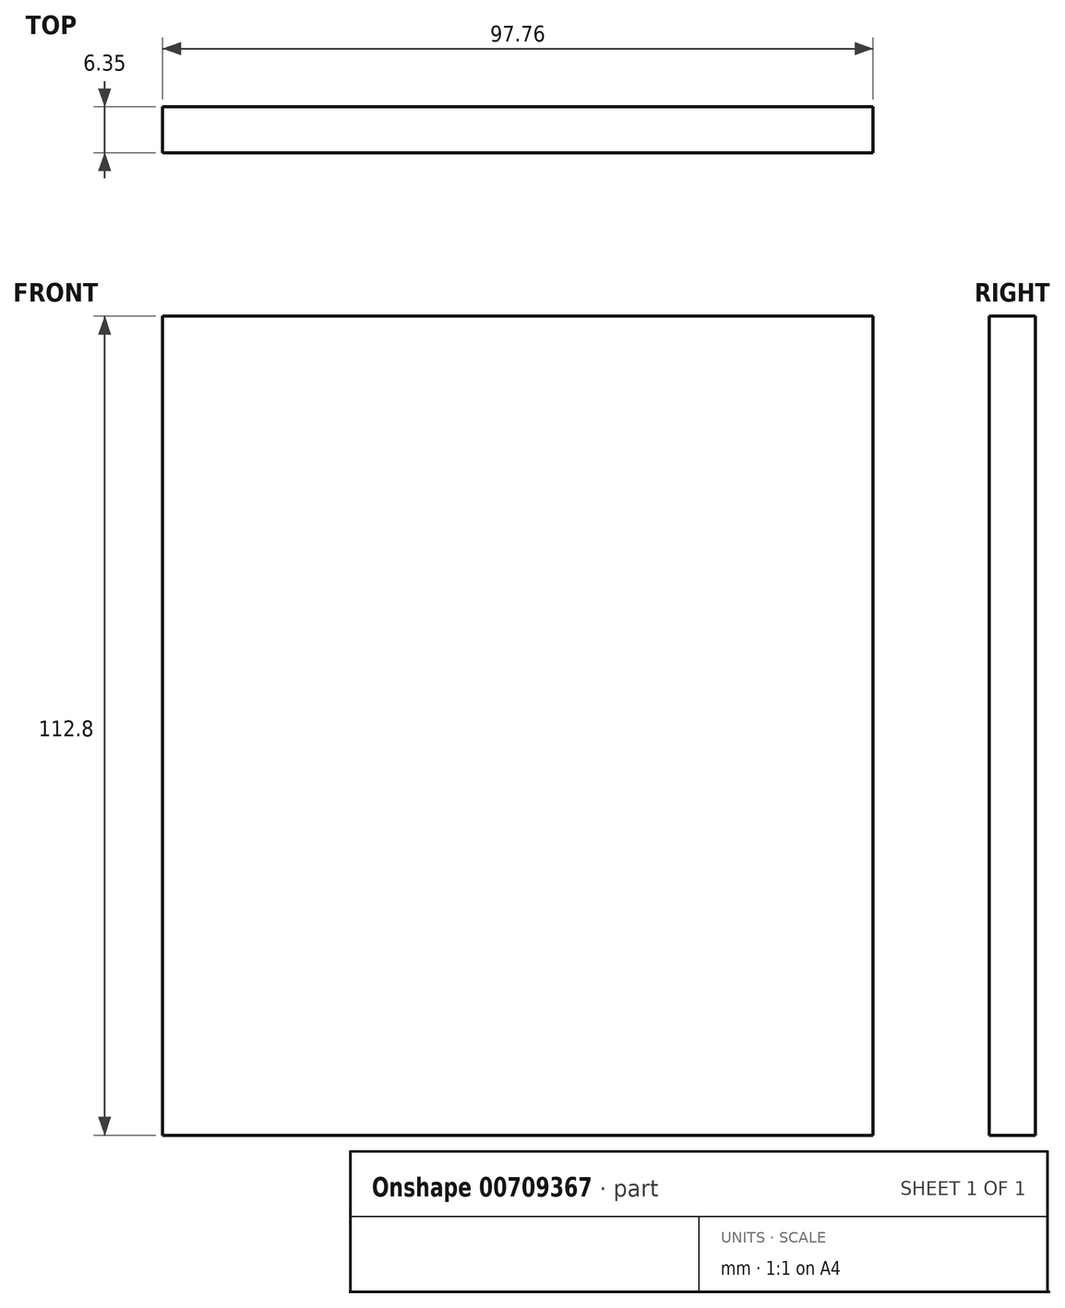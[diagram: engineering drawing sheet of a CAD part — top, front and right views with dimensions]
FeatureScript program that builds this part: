
annotation { "Feature Type Name" : "Feature", "Feature Type Description" : "" }
export const myFeature = defineFeature(function(context is Context, id is Id, definition is map)
    precondition{}
    {
        {
            var Q0;
            Q0=qCreatedBy(makeId("Front.planeOp"),FACE);
            var sketch = newSketch(context, id + "F0", { "sketchPlane" : qUnion([Q0])});
            skLineSegment(sketch, "E0.bottom", {"start": v(-48.88, 56.4) * mm, "end": v(48.88, 56.4) * mm});
            skLineSegment(sketch, "E0.top", {"start": v(-48.88, -56.4) * mm, "end": v(48.88, -56.4) * mm});
            skLineSegment(sketch, "E0.left", {"start": v(-48.88, 56.4) * mm, "end": v(-48.88, -56.4) * mm});
            skLineSegment(sketch, "E0.right", {"start": v(48.88, 56.4) * mm, "end": v(48.88, -56.4) * mm});
            skSolve(sketch);
        }
        {
            var Q0;
            Q0=makeQuery(id+"F0.imprint","IMPRINT",FACE,{"disambiguationData":[TD([[makeQuery(id+"F0.imprint","IMPRINT",EDGE,{"derivedFrom":sQuery(id+"F0.wireOp",EDGE,"E0.bottom")}),-1.0]])]});
            extrude(context, id + "F1", {"entities" : qUnion([Q0]), "depth" : 6.35 * mm, "offsetDistance" : 25.4 * mm});
        }
    });
